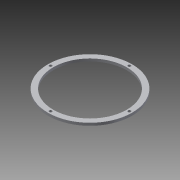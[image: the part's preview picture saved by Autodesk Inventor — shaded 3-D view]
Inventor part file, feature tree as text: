
AUTODESK INVENTOR PART (.ipt)
format: ipt  version: 2013 (Build 170138000, 138)  size: 88,576 bytes
history: native  units: in
note: dims shown in document units (in); Inventor stores cm internally (conversion verified against a paired STEP export)
features: extrude x1, sketch x1
ambient origin geometry x8: Origin, YZ Plane, XZ Plane, XY Plane, X Axis, Y Axis, Z Axis, Center Point
bodies: Solid1 (feature_tree)
feature tree (2):
  extrude  "Extrusion1"  Depth=8.0in
  sketch  "Sketch1"  dims[d0=7.0in d1=8.0in d2=7.5in d3=0.266in d4=1.5748in d6=360.0deg d8=0.25in d9=0.0in]
